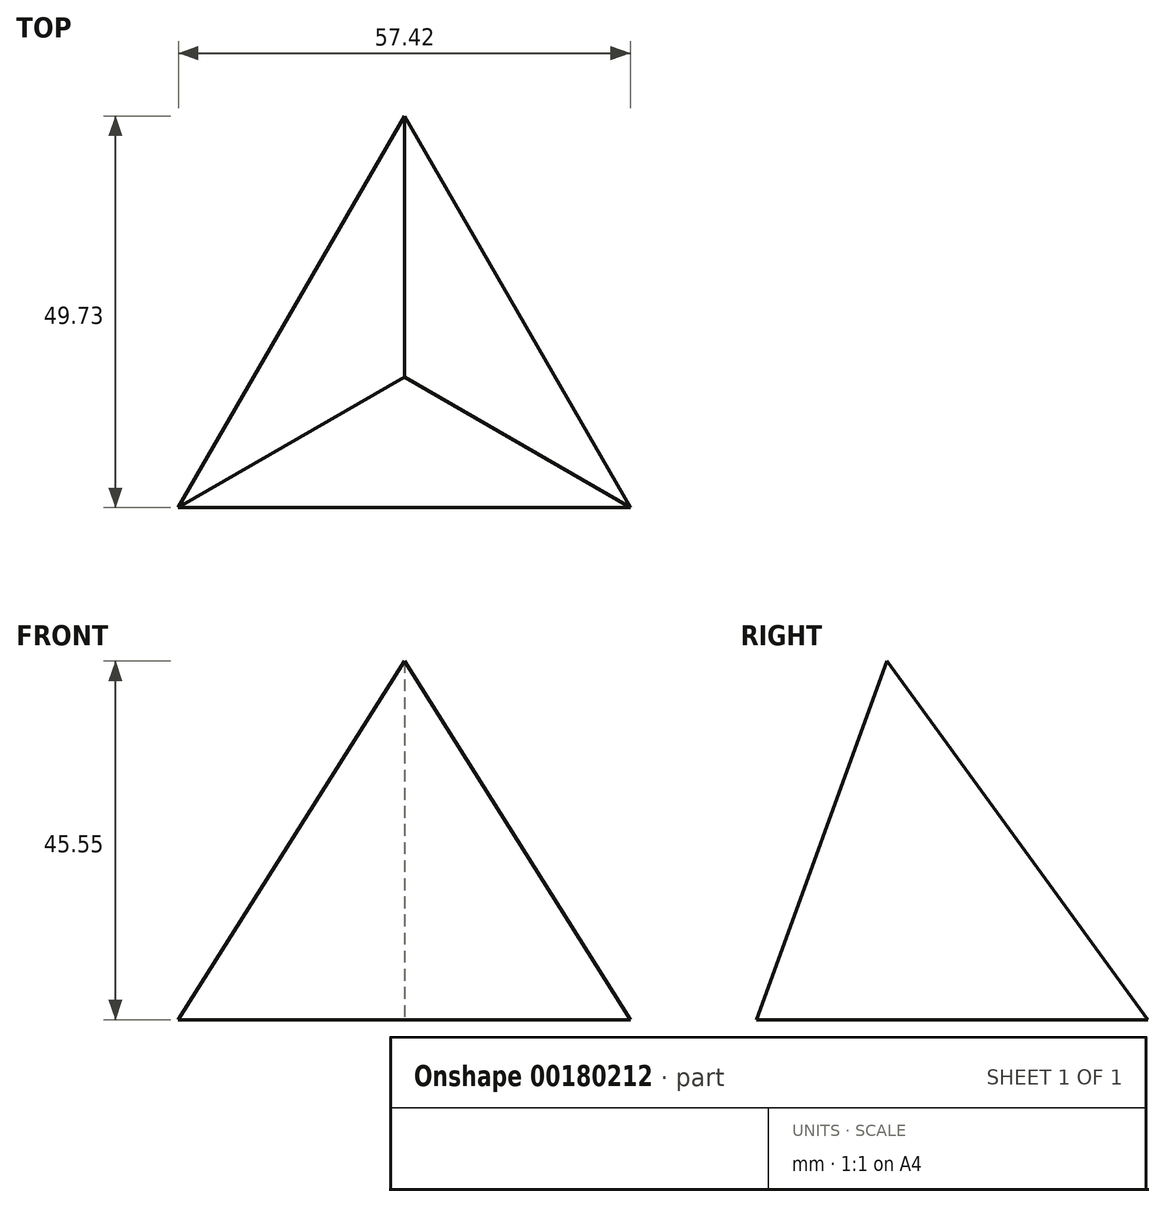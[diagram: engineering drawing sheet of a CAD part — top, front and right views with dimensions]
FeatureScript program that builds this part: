
annotation { "Feature Type Name" : "Feature", "Feature Type Description" : "" }
export const myFeature = defineFeature(function(context is Context, id is Id, definition is map)
    precondition{}
    {
        {
            var Q0;
            Q0=qCreatedBy(makeId("Top.planeOp"),FACE);
            var sketch = newSketch(context, id + "F0", { "sketchPlane" : qUnion([Q0])});
            skLineSegment(sketch, "E0.0", {"start": v(-12.7, -7.33) * mm, "end": v(0, 14.66) * mm});
            skLineSegment(sketch, "E0.1", {"start": v(0, 14.66) * mm, "end": v(12.7, -7.33) * mm});
            skLineSegment(sketch, "E0.2", {"start": v(12.7, -7.33) * mm, "end": v(-12.7, -7.33) * mm});
            skPoint(sketch, "E0.0.midPoint", {"position": v(-6.35, 3.67) * mm});
            skSolve(sketch);
        }
        {
            var Q0;
            Q0 = qSketchRegion(id + "F0", true);
            extrude(context, id + "F1", {"entities" : qUnion([Q0]), "depth" : 25.4 * mm, "hasDraft" : true, "draftAngle" : 20 * degree, "draftPullDirection" : true, "hasSecondDirection" : true, "secondDirectionOppositeDirection" : true, "secondDirectionDepth" : 25.4 * mm, "hasSecondDirectionDraft" : true, "secondDirectionDraftAngle" : 20 * degree});
        }
    });
